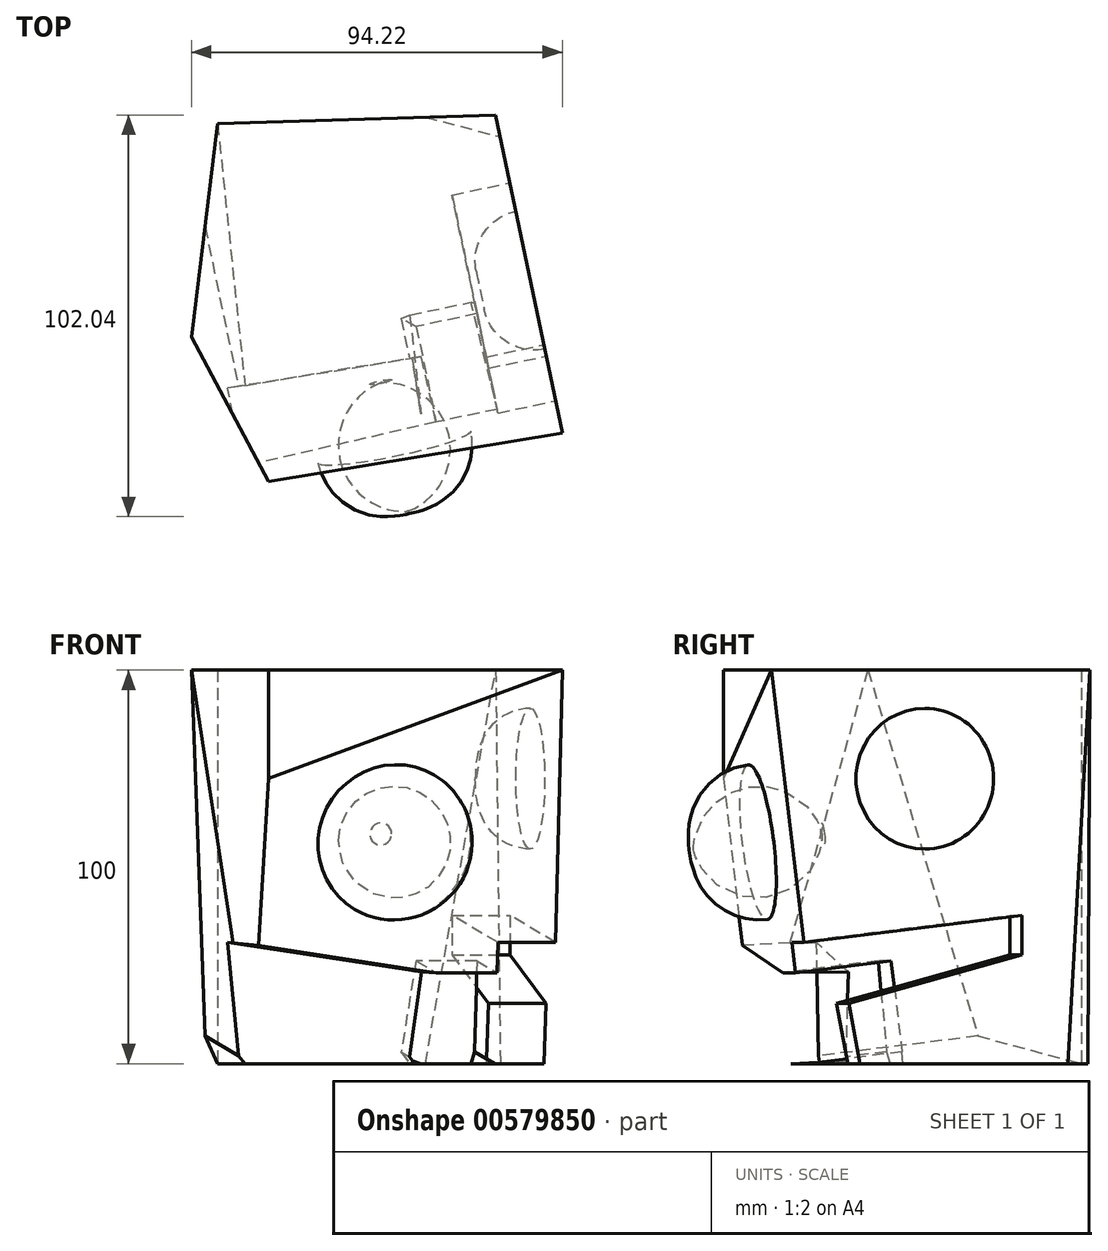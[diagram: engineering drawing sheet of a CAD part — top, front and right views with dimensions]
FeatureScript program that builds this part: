
annotation { "Feature Type Name" : "Feature", "Feature Type Description" : "" }
export const myFeature = defineFeature(function(context is Context, id is Id, definition is map)
    precondition{}
    {
        {
            var Q0;
            Q0=qCreatedBy(makeId("Top.planeOp"),FACE);
            var sketch = newSketch(context, id + "F0", { "sketchPlane" : qUnion([Q0])});
            skLineSegment(sketch, "E0", {"start": v(-27.94, -56.15) * mm, "end": v(46.7, -43.95) * mm});
            skLineSegment(sketch, "E1", {"start": v(46.7, -43.95) * mm, "end": v(29.77, 36.92) * mm});
            skLineSegment(sketch, "E2", {"start": v(29.77, 36.92) * mm, "end": v(-40.9, 34.71) * mm});
            skLineSegment(sketch, "E3", {"start": v(-40.9, 34.71) * mm, "end": v(-47.52, -19.46) * mm});
            skLineSegment(sketch, "E4", {"start": v(-47.52, -19.46) * mm, "end": v(-27.94, -56.15) * mm});
            skSolve(sketch);
        }
        {
            var Q0;
            Q0=qSketchRegion(id+"F0",true);
            extrude(context, id + "F1", {"entities" : qUnion([Q0]), "depth" : 100 * mm, "offsetDistance" : 25 * mm});
        }
        {
            var Q0;
            Q0=makeQuery(id+"F1.opExtrude","SWEPT_FACE",FACE,{"disambiguationData":[OSD([sQuery(id+"F0.wireOp",EDGE,"E2")])]});
            var sketch = newSketch(context, id + "F2", { "sketchPlane" : qUnion([Q0])});
            skLineSegment(sketch, "E5", {"start": v(-13.02, 0) * mm, "end": v(-30.91, 100) * mm});
            skLineSegment(sketch, "E6", {"start": v(-30.91, 100) * mm, "end": v(-30.91, 0) * mm});
            skLineSegment(sketch, "E7", {"start": v(-30.91, 0) * mm, "end": v(-13.02, 0) * mm});
            skSolve(sketch);
        }
        {
            var Q0;
            Q0=makeQuery(id+"F1.opExtrude","SWEPT_FACE",FACE,{"disambiguationData":[OSD([sQuery(id+"F0.wireOp",EDGE,"E1")])]});
            var sketch = newSketch(context, id + "F3", { "sketchPlane" : qUnion([Q0])});
            skLineSegment(sketch, "E8", {"start": v(-52.59, 100) * mm, "end": v(-44.17, 30.79) * mm});
            skLineSegment(sketch, "E9", {"start": v(-44.17, 30.79) * mm, "end": v(12.4, 37.67) * mm});
            skLineSegment(sketch, "E10", {"start": v(12.4, 37.67) * mm, "end": v(12.4, 27.61) * mm});
            skLineSegment(sketch, "E11", {"start": v(12.4, 27.61) * mm, "end": v(-32.56, 15.34) * mm});
            skLineSegment(sketch, "E12", {"start": v(-32.56, 15.34) * mm, "end": v(-29.64, 0) * mm});
            skLineSegment(sketch, "E13", {"start": v(-29.64, 0) * mm, "end": v(24.37, 0) * mm});
            skLineSegment(sketch, "E14", {"start": v(24.37, 0) * mm, "end": v(30.04, 100) * mm});
            skLineSegment(sketch, "E15", {"start": v(30.04, 100) * mm, "end": v(-52.59, 100) * mm});
            skCircle(sketch, "E16", {"center": v(-12.82, 72.4) * mm, "radius": 17.86 * mm});
            skSolve(sketch);
        }
        {
            var Q0;
            Q0=sQuery(id+"F3.wireOp",VERTEX,"E13.end");
            var Q1;
            Q1=sQuery(id+"F2.wireOp",VERTEX,"E5.start");
            var Q2;
            Q2=sQuery(id+"F3.wireOp",VERTEX,"E14.end");
            cPlane(context, id + "F4", {"entities" : qUnion([Q0, Q1, Q2]), "cplaneType" : CPlaneType.THREE_POINT, "offset" : 25 * mm, "width" : 150 * mm, "height" : 150 * mm});
        }
        {
            var Q0;
            Q0=qCreatedBy(id+"F4.planeOp",FACE);
            var sketch = newSketch(context, id + "F5", { "sketchPlane" : qUnion([Q0])});
            skPoint(sketch, "E17.0", {"position": v(2.32, 1.9) * mm});
            skPoint(sketch, "E17.1", {"position": v(22, 1.64) * mm});
            skPoint(sketch, "E17.2", {"position": v(20.8, 101.8) * mm});
            skLineSegment(sketch, "E18", {"start": v(20.8, 101.8) * mm, "end": v(22, 1.64) * mm});
            skLineSegment(sketch, "E19", {"start": v(2.32, 1.9) * mm, "end": v(22, 1.64) * mm});
            skLineSegment(sketch, "E20", {"start": v(2.32, 1.9) * mm, "end": v(20.8, 101.8) * mm});
            skSolve(sketch);
        }
        {
            var Q0;
            Q0=qSketchRegion(id+"F5",true);
            extrude(context, id + "F6", {"entities" : qUnion([Q0]), "operationType" : NewBodyOperationType.REMOVE, "oppositeDirection" : true, "depth" : 25 * mm, "offsetDistance" : 25 * mm});
        }
        {
            var Q0;
            Q0=makeQuery(id+"F3.imprint","IMPRINT",FACE,{"disambiguationData":[TD([[makeQuery(id+"F3.imprint","IMPRINT",EDGE,{"derivedFrom":sQuery(id+"F3.wireOp",EDGE,"E8")}),-1.0]])]});
            extrude(context, id + "F7", {"entities" : qUnion([Q0]), "operationType" : NewBodyOperationType.REMOVE, "oppositeDirection" : true, "depth" : 15 * mm, "offsetDistance" : 25 * mm});
        }
        {
            var Q0;
            Q0=makeQuery(id+"F7.boolean.opBoolean","COPY",FACE,{"derivedFrom":makeQuery(id+"F7.opExtrude","SWEPT_FACE",FACE,{"disambiguationData":[OSD([sQuery(id+"F3.wireOp",EDGE,"E8")])]})});
            var sketch = newSketch(context, id + "F8", { "sketchPlane" : qUnion([Q0])});
            skLineSegment(sketch, "E21.0", {"start": v(-79.54, 107.67) * mm, "end": v(-82.47, -8.18) * mm});
            skPoint(sketch, "E22.0", {"position": v(39.36, 104.66) * mm});
            skPoint(sketch, "E22.1", {"position": v(37.6, 34.95) * mm});
            skLineSegment(sketch, "E23", {"start": v(39.36, 104.66) * mm, "end": v(-79.54, 107.67) * mm});
            skLineSegment(sketch, "E24", {"start": v(-82.47, -8.18) * mm, "end": v(37.6, -11.21) * mm});
            skLineSegment(sketch, "E25", {"start": v(37.6, -11.21) * mm, "end": v(37.6, 34.95) * mm});
            skLineSegment(sketch, "E26", {"start": v(37.6, 34.95) * mm, "end": v(-81.3, 37.96) * mm});
            skSolve(sketch);
        }
        {
            var Q0;
            {var subQ5=sQuery(id+"F3.wireOp",EDGE,"E8");var subQ6=makeQuery(id+"F7.boolean.opBoolean","COPY",EDGE,{"derivedFrom":makeQuery(id+"F7.opExtrude","CAP_EDGE",EDGE,{"disambiguationData":[OSD([subQ5])],"isStart":false})});Q0=makeQuery(id+"F8.imprint","IMPRINT",FACE,{"disambiguationData":[TD([[makeQuery(id+"F8.imprint","IMPRINT",EDGE,{"derivedFrom":subQ6}),-1.0]])]});}
            var Q1;
            {var subQ1=sQuery(id+"F8.wireOp",EDGE,"E24");Q1=makeQuery(id+"F8.imprint","IMPRINT",FACE,{"disambiguationData":[TD([[makeQuery(id+"F8.imprint","IMPRINT",EDGE,{"derivedFrom":subQ1}),1.0]])]});}
            extrude(context, id + "F9", {"entities" : qUnion([Q0, Q1]), "operationType" : NewBodyOperationType.REMOVE, "depth" : 25 * mm, "offsetDistance" : 25 * mm});
        }
        {
            var Q0;
            Q0=makeQuery(id+"F3.imprint","IMPRINT",FACE,{"disambiguationData":[TD([[makeQuery(id+"F3.imprint","IMPRINT",EDGE,{"derivedFrom":sQuery(id+"F3.wireOp",EDGE,"E16")}),1.0]])]});
            extrude(context, id + "F10", {"entities" : qUnion([Q0]), "operationType" : NewBodyOperationType.REMOVE, "oppositeDirection" : true, "depth" : 13 * mm, "offsetDistance" : 25 * mm});
        }
        {
            var Q0;
            Q0=makeQuery(id+"F10.boolean.opBoolean","COPY",EDGE,{"derivedFrom":makeQuery(id+"F10.opExtrude","CAP_EDGE",EDGE,{"disambiguationData":[OSD([sQuery(id+"F3.wireOp",EDGE,"E16")])],"isStart":false})});
            fillet(context, id + "F11", {"entities" : qUnion([Q0]), "radius" : 13 * mm, "tangentPropagation" : true, "allowEdgeOverflow" : false});
        }
        {
            var Q0;
            {var subQ0=sQuery(id+"F3.wireOp",EDGE,"E8");Q0=makeQuery(id+"F9.boolean.opBoolean","MERGE",FACE,{"derivedFrom":[makeQuery(id+"F7.boolean.opBoolean","COPY",FACE,{"derivedFrom":makeQuery(id+"F7.opExtrude","SWEPT_FACE",FACE,{"disambiguationData":[OSD([subQ0])]})})],"fromTools":[makeQuery(id+"F9.opExtrude","CAP_FACE",FACE,{"disambiguationData":[OSD([sQuery(id+"F0.wireOp",EDGE,"E0"),subQ0,sQuery(id+"F8.wireOp",EDGE,"E21.0"),sQuery(id+"F8.wireOp",EDGE,"E23"),sQuery(id+"F8.wireOp",EDGE,"E24"),sQuery(id+"F8.wireOp",EDGE,"E25"),sQuery(id+"F8.wireOp",EDGE,"E26")])],"isStart":true})]});}
            var sketch = newSketch(context, id + "F12", { "sketchPlane" : qUnion([Q0])});
            skLineSegment(sketch, "E27.0", {"start": v(22.6, 35.33) * mm, "end": v(21.82, 4.33) * mm});
            skLineSegment(sketch, "E27.1", {"start": v(39.11, 94.68) * mm, "end": v(36.6, -4.55) * mm});
            skLineSegment(sketch, "E27.2", {"start": v(22.6, 35.33) * mm, "end": v(37.6, 34.95) * mm});
            skLineSegment(sketch, "E27.3", {"start": v(36.6, -4.55) * mm, "end": v(18.98, -4.48) * mm});
            skLineSegment(sketch, "E27.4", {"start": v(-41.28, 5.93) * mm, "end": v(21.82, 4.33) * mm});
            skLineSegment(sketch, "E27.5", {"start": v(18.98, -4.48) * mm, "end": v(-33.03, -4.28) * mm});
            skLineSegment(sketch, "E27.6", {"start": v(-33.03, -4.28) * mm, "end": v(-50.45, 2.4) * mm});
            skLineSegment(sketch, "E27.7", {"start": v(-50.45, 2.4) * mm, "end": v(-41.28, 5.93) * mm});
            skLineSegment(sketch, "E27.8", {"start": v(-47.95, 101.64) * mm, "end": v(-50.45, 2.4) * mm});
            skLineSegment(sketch, "E27.9", {"start": v(-47.95, 101.64) * mm, "end": v(-36.18, 106.16) * mm});
            skLineSegment(sketch, "E27.10", {"start": v(-36.18, 106.16) * mm, "end": v(39.36, 104.66) * mm});
            skLineSegment(sketch, "E27.11", {"start": v(39.36, 104.66) * mm, "end": v(-36.87, 78.82) * mm});
            skLineSegment(sketch, "E27.12", {"start": v(-36.18, 106.16) * mm, "end": v(-36.87, 78.82) * mm});
            skLineSegment(sketch, "E27.13", {"start": v(-36.87, 78.82) * mm, "end": v(-41.28, 5.93) * mm});
            skLineSegment(sketch, "E28", {"start": v(-47.95, 101.64) * mm, "end": v(-41.28, 5.93) * mm});
            skLineSegment(sketch, "E29", {"start": v(-41.28, 5.93) * mm, "end": v(-33.03, -4.28) * mm});
            skLineSegment(sketch, "E30", {"start": v(22.41, 27.61) * mm, "end": v(6.63, 28) * mm});
            skLineSegment(sketch, "E31", {"start": v(6.63, 28) * mm, "end": v(2.7, 4.81) * mm});
            skLineSegment(sketch, "E32", {"start": v(2.7, 4.81) * mm, "end": v(9.44, -4.45) * mm});
            skLineSegment(sketch, "E33", {"start": v(18.98, -4.48) * mm, "end": v(21.82, 4.33) * mm});
            skCircle(sketch, "E34", {"center": v(-4.22, 61.71) * mm, "radius": 19.81 * mm});
            skSolve(sketch);
        }
        {
            var Q0;
            {var subQ3=sQuery(id+"F12.wireOp",EDGE,"E30");Q0=makeQuery(id+"F12.imprint","IMPRINT",FACE,{"disambiguationData":[TD([[makeQuery(id+"F12.imprint","IMPRINT",EDGE,{"derivedFrom":subQ3}),1.0]])]});}
            var Q1;
            {var subQ2=sQuery(id+"F12.wireOp",EDGE,"E32");Q1=makeQuery(id+"F12.imprint","IMPRINT",FACE,{"disambiguationData":[TD([[makeQuery(id+"F12.imprint","IMPRINT",EDGE,{"derivedFrom":subQ2}),1.0]])]});}
            extrude(context, id + "F13", {"entities" : qUnion([Q0, Q1]), "operationType" : NewBodyOperationType.REMOVE, "oppositeDirection" : true, "depth" : 25 * mm, "offsetDistance" : 25 * mm});
        }
        {
            var Q0;
            Q0=makeQuery(id+"F12.imprint","IMPRINT",FACE,{"disambiguationData":[TD([[makeQuery(id+"F12.imprint","IMPRINT",EDGE,{"derivedFrom":sQuery(id+"F12.wireOp",EDGE,"E27.7")}),1.0]])]});
            var Q1;
            Q1=makeQuery(id+"F12.imprint","IMPRINT",FACE,{"disambiguationData":[TD([[makeQuery(id+"F12.imprint","IMPRINT",EDGE,{"derivedFrom":sQuery(id+"F12.wireOp",EDGE,"E27.6")}),-1.0]])]});
            extrude(context, id + "F14", {"entities" : qUnion([Q0, Q1]), "operationType" : NewBodyOperationType.REMOVE, "oppositeDirection" : true, "depth" : 90 * mm, "offsetDistance" : 25 * mm});
        }
        {
            var Q0;
            Q0=makeQuery(id+"F12.imprint","IMPRINT",FACE,{"disambiguationData":[TD([[makeQuery(id+"F12.imprint","IMPRINT",EDGE,{"derivedFrom":sQuery(id+"F12.wireOp",EDGE,"E34")}),1.0]])]});
            extrude(context, id + "F15", {"entities" : qUnion([Q0]), "operationType" : NewBodyOperationType.REMOVE, "oppositeDirection" : true, "depth" : 17 * mm, "offsetDistance" : 25 * mm});
        }
        {
            var Q0;
            Q0=makeQuery(id+"F15.boolean.opBoolean","COPY",EDGE,{"derivedFrom":makeQuery(id+"F15.opExtrude","CAP_EDGE",EDGE,{"disambiguationData":[OSD([sQuery(id+"F12.wireOp",EDGE,"E34")])],"isStart":false})});
            fillet(context, id + "F16", {"entities" : qUnion([Q0]), "radius" : 17 * mm, "tangentPropagation" : true, "allowEdgeOverflow" : false});
        }
        {
            var Q0;
            Q0=makeQuery(id+"F1.opExtrude","SWEPT_FACE",FACE,{"disambiguationData":[OSD([sQuery(id+"F0.wireOp",EDGE,"E0")])]});
            var sketch = newSketch(context, id + "F17", { "sketchPlane" : qUnion([Q0])});
            skPoint(sketch, "E35.0", {"position": v(7.83, 23.12) * mm});
            skLineSegment(sketch, "E35.1", {"start": v(-50.04, 100) * mm, "end": v(-42.15, 7.03) * mm});
            skLineSegment(sketch, "E35.2", {"start": v(-42.15, 7.03) * mm, "end": v(-39.59, 0) * mm});
            skLineSegment(sketch, "E35.3", {"start": v(-39.59, 0) * mm, "end": v(4.36, 0) * mm});
            skLineSegment(sketch, "E35.4", {"start": v(7.83, 23.12) * mm, "end": v(4.36, 0) * mm});
            skLineSegment(sketch, "E36", {"start": v(7.83, 23.12) * mm, "end": v(-44.18, 30.93) * mm});
            skSolve(sketch);
        }
        {
            var Q0;
            {var subQ0=sQuery(id+"F17.wireOp",EDGE,"E35.2");Q0=makeQuery(id+"F17.imprint","IMPRINT",FACE,{"disambiguationData":[TD([[makeQuery(id+"F17.imprint","IMPRINT",EDGE,{"derivedFrom":subQ0}),1.0]])]});}
            extrude(context, id + "F18", {"entities" : qUnion([Q0]), "operationType" : NewBodyOperationType.REMOVE, "oppositeDirection" : true, "depth" : 25 * mm, "offsetDistance" : 25 * mm});
        }
    });
